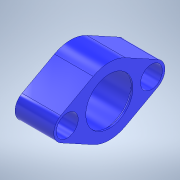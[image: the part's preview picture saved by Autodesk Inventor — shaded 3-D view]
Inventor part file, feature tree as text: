
AUTODESK INVENTOR PART (.ipt)
format: ipt  version: 2022 (Build 260153000, 153)  size: 160,768 bytes
history: native  units: in
note: dims shown in document units (in); Inventor stores cm internally (conversion verified against a paired STEP export)
features: sketch x5, hole x2, chamfer x2, plane x1, extrude x1
ambient origin geometry x8: Origin, YZ Plane, XZ Plane, XY Plane, X Axis, Y Axis, Z Axis, Center Point
bodies: Body1 (feature_tree)
feature tree (11):
  plane  "Work Plane1"
  extrude  "Extrusion1"  Depth=0.4528in TaperAngle=0.0deg
  hole  "Hole2"  [1 undecoded]
  hole  "Hole1"  [1 undecoded]
  chamfer  "Chamfer2"  Distance=0.0197in
  chamfer  "Chamfer1"  Distance=0.0394in
  sketch  "Sketch1"  dims[d0=-0.3937in d1=0.4528in d2=0.0in]
  sketch  "Sketch2"  dims[d3=0.5512in d4=0.2362in d5=0.1575in d6=0.0787in d7=90.0deg d8=0.315in d9=0.8108in]
  sketch  "Sketch3"  dims[d10=0.126in d11=0.2362in d12=0.2559in d13=0.2362in d14=90.0deg d15=0.315in d16=0.0in]
  sketch  "Sketch4"  dims[d17=0.126in d18=0.2362in d19=0.2559in d20=0.2362in d21=90.0deg d22=0.315in d23=0.0in]
  sketch  "Sketch5"  dims[d24=0.6299in d25=0.2362in d26=0.1575in d27=0.0787in d28=90.0deg d29=0.3937in d30=0.6184in d31=0.0197in d32=0.0197in d33=17.7165in d34=0.0197in d35=0.0197in d36=17.7165in d37=0.0197in d38=0.0197in d39=17.7165in d40=0.0394in d41=0.0394in d42=0.0394in d43=0.0059in d44=0.0098in d45=0.0148in d46=32.2835in d47=0.0295in d48=46.4567in d49=0.0025in d50=0.0295in d51=0.0148in]
note: 2 required parameter values undecoded (feature->parameter linkage not recoverable at this tier; creation-order binding heuristic only, values carry confidence <= 0.55)
